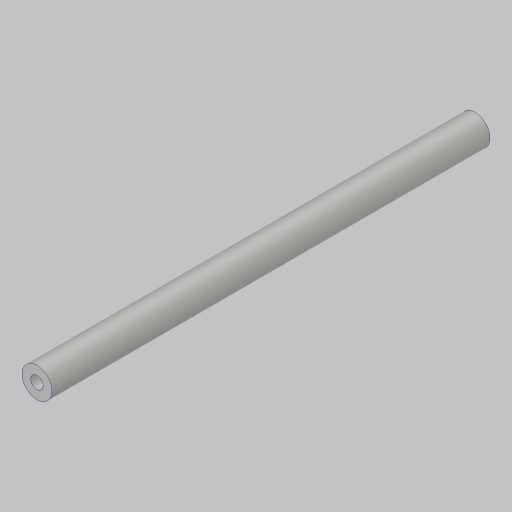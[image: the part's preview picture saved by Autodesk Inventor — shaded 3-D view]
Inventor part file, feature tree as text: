
AUTODESK INVENTOR PART (.ipt)
format: ipt  version: 2023.5 (Build 275446000, 446)  size: 103,936 bytes
history: native  units: in
note: dims shown in document units (in); Inventor stores cm internally (conversion verified against a paired STEP export)
features: extrude x1, hole x1
ambient origin geometry x8: Origin, YZ Plane, XZ Plane, XY Plane, X Axis, Y Axis, Z Axis, Center Point
bodies: Solid1 (feature_tree)
feature tree (2):
  extrude  "Extrusion1"  Depth=5.5in
  hole  "Hole1"  [1 undecoded]
note: 1 required parameter value undecoded (feature->parameter linkage not recoverable at this tier; creation-order binding heuristic only, values carry confidence <= 0.55)
